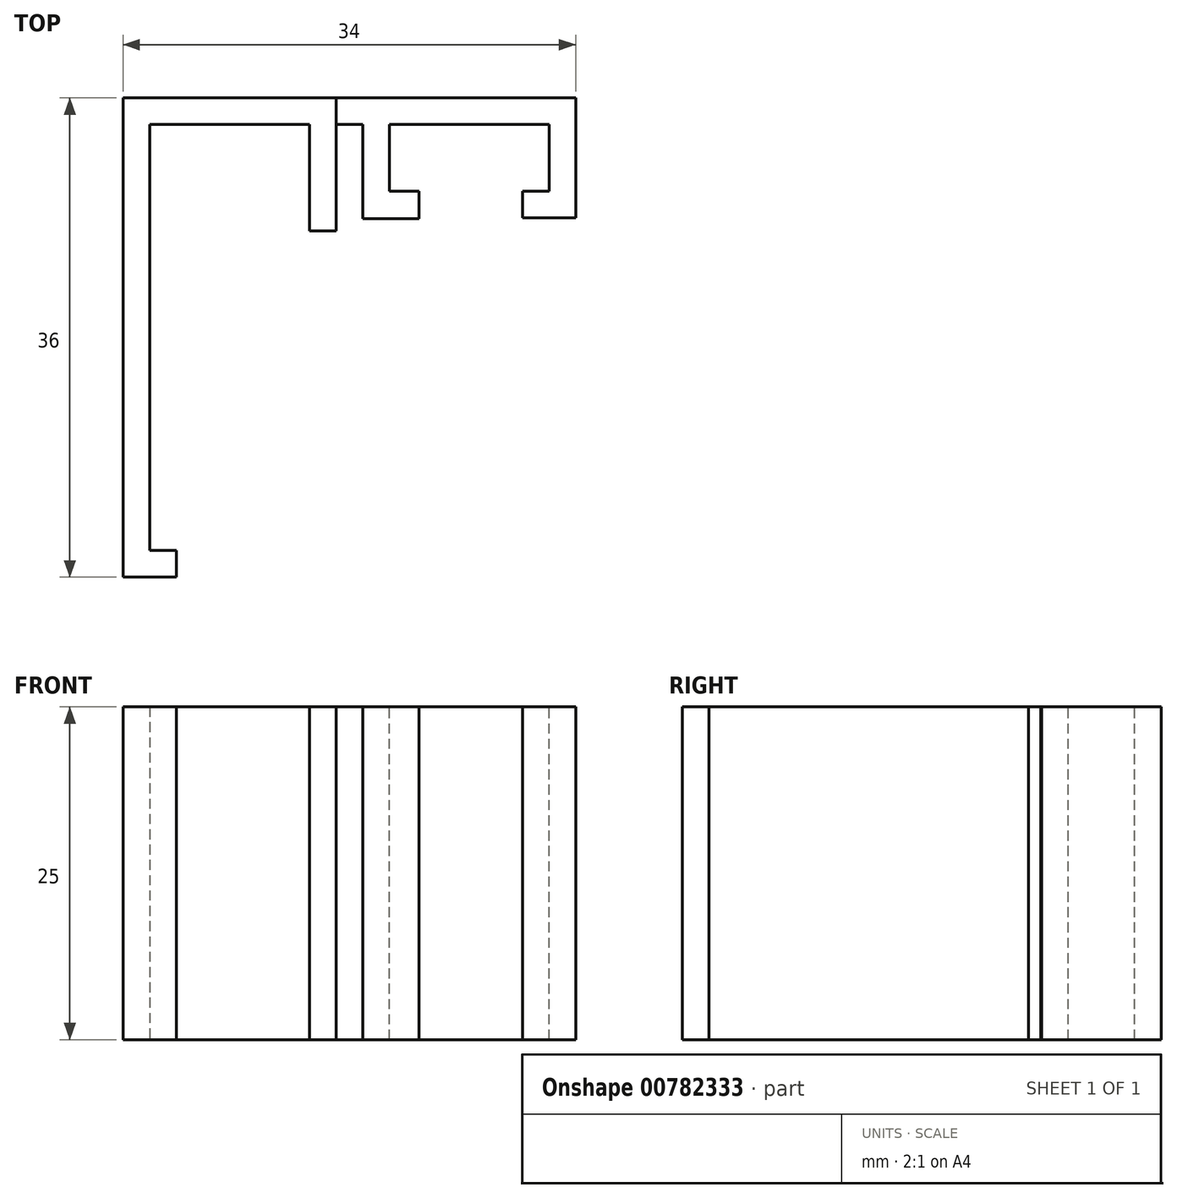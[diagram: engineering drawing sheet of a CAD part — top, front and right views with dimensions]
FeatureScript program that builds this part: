
annotation { "Feature Type Name" : "Feature", "Feature Type Description" : "" }
export const myFeature = defineFeature(function(context is Context, id is Id, definition is map)
    precondition{}
    {
        {
            var Q0;
            Q0=qCreatedBy(makeId("Top.planeOp"),FACE);
            var sketch = newSketch(context, id + "F0", { "sketchPlane" : qUnion([Q0])});
            skLineSegment(sketch, "E0.bottom", {"start": v(1, 17) * mm, "end": v(-1, 17) * mm});
            skLineSegment(sketch, "E0.left", {"start": v(1, 15) * mm, "end": v(1, -17) * mm});
            skLineSegment(sketch, "E0.right", {"start": v(-1, 17) * mm, "end": v(-1, -17) * mm});
            skPoint(sketch, "E0.middle", {"position": v(0, 0) * mm});
            skLineSegment(sketch, "E1.bottom", {"start": v(-1, 17) * mm, "end": v(15, 17) * mm});
            skLineSegment(sketch, "E1.top", {"start": v(1, 15) * mm, "end": v(13, 15) * mm});
            skLineSegment(sketch, "E1.left", {"start": v(-1, 17) * mm, "end": v(-1, 15) * mm});
            skLineSegment(sketch, "E1.right", {"start": v(15, 17) * mm, "end": v(15, 15) * mm});
            skLineSegment(sketch, "E2.bottom", {"start": v(15, 17) * mm, "end": v(13, 17) * mm});
            skLineSegment(sketch, "E2.top", {"start": v(15, 7) * mm, "end": v(13, 7) * mm});
            skLineSegment(sketch, "E2.left", {"start": v(15, 17) * mm, "end": v(15, 7) * mm});
            skLineSegment(sketch, "E2.right", {"start": v(13, 15) * mm, "end": v(13, 7) * mm});
            skLineSegment(sketch, "E3.bottom", {"start": v(1, -17) * mm, "end": v(3, -17) * mm});
            skLineSegment(sketch, "E3.top", {"start": v(-1, -19) * mm, "end": v(3, -19) * mm});
            skLineSegment(sketch, "E3.left", {"start": v(-1, -17) * mm, "end": v(-1, -19) * mm});
            skLineSegment(sketch, "E3.right", {"start": v(3, -17) * mm, "end": v(3, -19) * mm});
            skSolve(sketch);
        }
        {
            var Q0;
            Q0=makeQuery(id+"F0.imprint","IMPRINT",FACE,{"disambiguationData":[TD([[makeQuery(id+"F0.imprint","IMPRINT",EDGE,{"derivedFrom":sQuery(id+"F0.wireOp",EDGE,"E0.left")}),-1.0]])]});
            extrude(context, id + "F1", {"entities" : qUnion([Q0]), "depth" : 25 * mm, "offsetDistance" : 25 * mm});
        }
        {
            var Q0;
            Q0=makeQuery(id+"F1.opExtrude","CAP_FACE",FACE,{"disambiguationData":[OSD([sQuery(id+"F0.wireOp",EDGE,"E0.left"),sQuery(id+"F0.wireOp",EDGE,"E0.right"),sQuery(id+"F0.wireOp",EDGE,"E1.bottom"),sQuery(id+"F0.wireOp",EDGE,"E1.top"),sQuery(id+"F0.wireOp",EDGE,"E1.left"),sQuery(id+"F0.wireOp",EDGE,"E2.bottom"),sQuery(id+"F0.wireOp",EDGE,"E2.top"),sQuery(id+"F0.wireOp",EDGE,"E2.left"),sQuery(id+"F0.wireOp",EDGE,"E2.right"),sQuery(id+"F0.wireOp",EDGE,"E3.bottom"),sQuery(id+"F0.wireOp",EDGE,"E3.top"),sQuery(id+"F0.wireOp",EDGE,"E3.left"),sQuery(id+"F0.wireOp",EDGE,"E3.right")])],"isStart":false});
            var sketch = newSketch(context, id + "F2", { "sketchPlane" : qUnion([Q0])});
            skLineSegment(sketch, "E4.bottom", {"start": v(15, 17) * mm, "end": v(33, 17) * mm});
            skLineSegment(sketch, "E4.top", {"start": v(15, 15) * mm, "end": v(17, 15) * mm});
            skLineSegment(sketch, "E4.left", {"start": v(15, 17) * mm, "end": v(15, 15) * mm});
            skLineSegment(sketch, "E4.right", {"start": v(33, 17) * mm, "end": v(33, 15) * mm});
            skLineSegment(sketch, "E5.top", {"start": v(33, 8) * mm, "end": v(31, 8) * mm});
            skLineSegment(sketch, "E5.left", {"start": v(33, 15) * mm, "end": v(33, 8) * mm});
            skLineSegment(sketch, "E5.right", {"start": v(31, 15) * mm, "end": v(31, 10) * mm});
            skLineSegment(sketch, "E6.bottom", {"start": v(33, 8) * mm, "end": v(29, 8) * mm});
            skLineSegment(sketch, "E6.top", {"start": v(31, 10) * mm, "end": v(29, 10) * mm});
            skLineSegment(sketch, "E6.left", {"start": v(33, 8) * mm, "end": v(33, 10) * mm});
            skLineSegment(sketch, "E6.right", {"start": v(29, 8) * mm, "end": v(29, 10) * mm});
            skLineSegment(sketch, "E7.left", {"start": v(15, 15) * mm, "end": v(15, 7.93) * mm});
            skLineSegment(sketch, "E7.right", {"start": v(19, 15) * mm, "end": v(19, 10) * mm});
            skLineSegment(sketch, "E8.top", {"start": v(17, 7.93) * mm, "end": v(19, 7.93) * mm});
            skLineSegment(sketch, "E8.left", {"start": v(17, 15) * mm, "end": v(17, 7.93) * mm});
            skLineSegment(sketch, "E9.bottom", {"start": v(19, 7.93) * mm, "end": v(21.22, 7.93) * mm});
            skLineSegment(sketch, "E9.top", {"start": v(19, 10) * mm, "end": v(21.22, 10) * mm});
            skLineSegment(sketch, "E9.right", {"start": v(21.22, 7.93) * mm, "end": v(21.22, 10) * mm});
            skLineSegment(sketch, "E10.trimOffspring", {"start": v(19, 15) * mm, "end": v(31, 15) * mm});
            skSolve(sketch);
        }
        {
            var Q0;
            Q0=makeQuery(id+"F2.imprint","IMPRINT",FACE,{"disambiguationData":[TD([[makeQuery(id+"F2.imprint","IMPRINT",EDGE,{"derivedFrom":sQuery(id+"F2.wireOp",EDGE,"E4.bottom")}),-1.0]])]});
            extrude(context, id + "F3", {"entities" : qUnion([Q0]), "oppositeDirection" : true, "depth" : 25 * mm, "offsetDistance" : 25 * mm});
        }
    });
